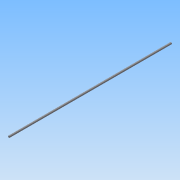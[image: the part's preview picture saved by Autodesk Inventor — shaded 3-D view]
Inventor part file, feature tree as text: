
AUTODESK INVENTOR PART (.ipt)
format: ipt  version: 2015 (Build 190159000, 159)  size: 64,000 bytes
history: native  units: mm
features: extrude x1, sketch x1
ambient origin geometry x8: Origin, YZ Plane, XZ Plane, XY Plane, X Axis, Y Axis, Z Axis, Center Point
bodies: Solid1 (feature_tree)
feature tree (2):
  extrude  "Extrusion1"  Depth=450.0mm TaperAngle=0.0deg
  sketch  "Sketch1"  dims[d0=5.0mm d1=450.0mm d2=0.0mm]
